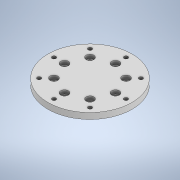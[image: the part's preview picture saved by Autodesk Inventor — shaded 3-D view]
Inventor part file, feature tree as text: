
AUTODESK INVENTOR PART (.ipt)
format: ipt  version: 2021 (Build 250183000, 183)  size: 193,536 bytes
history: native  units: mm
features: sketch x3, projected_geometry x3, hole x2, revolve x1, plane x1, extrude x1, chamfer x1
ambient origin geometry x8: Origin, YZ Plane, XZ Plane, XY Plane, X Axis, Y Axis, Z Axis, Center Point
bodies: Solid1 (feature_tree)
feature tree (12):
  revolve  "Revolution1"  [1 undecoded]
  sketch  "Sketch2"  dims[d3=12.0mm d4=1.0mm]
  hole  "Hole1"  [1 undecoded]
  hole  "Hole2"  [1 undecoded]
  plane  "Work Plane1"
  extrude  "Extrusion1"  Depth=2.0mm
  chamfer  "Chamfer1"  Distance=80.0mm Angle=360.0deg
  sketch  "Sketch1"  dims[d0=6.0mm d2=5.0mm]
  projected_geometry  "Projected Loop1"
  projected_geometry  "Projected Loop2"
  sketch  "Sketch3"  dims[d5=90.0deg d6=42.5mm d7=60.0mm d8=80.0mm d10=360.0deg d12=35.0mm d13=3.4mm d14=6.0mm d15=6.5mm d16=3.0mm d17=90.0deg d18=8.0mm d19=20.594885mm d20=3.242mm d21=8.0mm d22=6.5mm d23=3.0mm d24=90.0deg d25=8.0mm d26=20.594885mm d27=4.0mm d29=5.0mm d30=2.0mm d31=0.0mm d32=0.5mm d33=2.0mm d34=45.0deg]
  projected_geometry  "Projected Loop3"
note: 3 required parameter values undecoded (feature->parameter linkage not recoverable at this tier; creation-order binding heuristic only, values carry confidence <= 0.55)